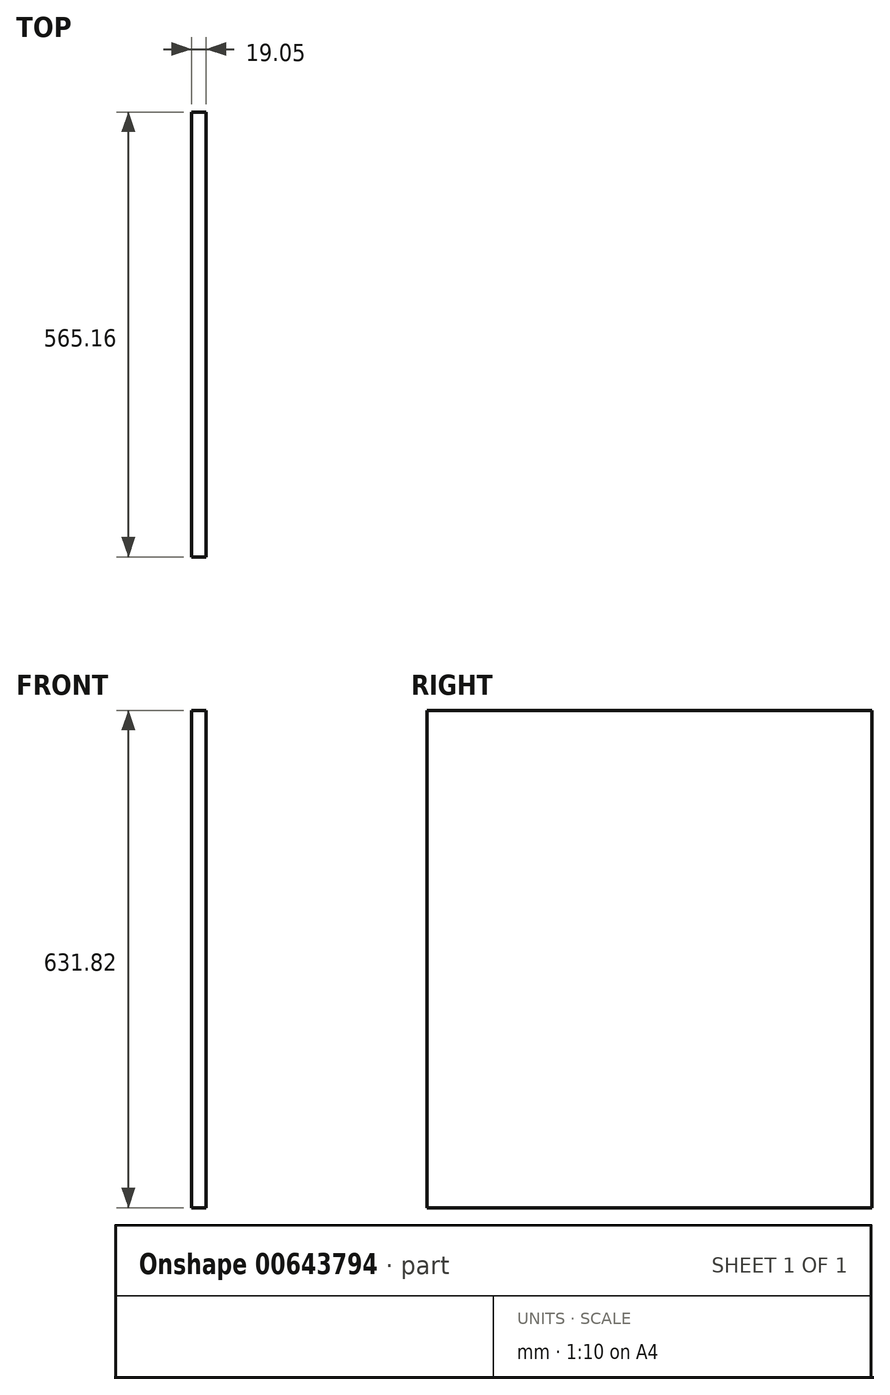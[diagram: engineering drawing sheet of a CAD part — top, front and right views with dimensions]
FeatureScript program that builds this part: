
annotation { "Feature Type Name" : "Feature", "Feature Type Description" : "" }
export const myFeature = defineFeature(function(context is Context, id is Id, definition is map)
    precondition{}
    {
        {
            var Q0;
            Q0=qCreatedBy(makeId("Right.planeOp"),FACE);
            var sketch = newSketch(context, id + "F0", { "sketchPlane" : qUnion([Q0])});
            skLineSegment(sketch, "E0.bottom", {"start": v(282.57, 315.91) * mm, "end": v(-282.58, 315.91) * mm});
            skLineSegment(sketch, "E0.top", {"start": v(282.57, -315.91) * mm, "end": v(-282.58, -315.91) * mm});
            skLineSegment(sketch, "E0.left", {"start": v(282.58, 315.91) * mm, "end": v(282.57, -315.91) * mm});
            skLineSegment(sketch, "E0.right", {"start": v(-282.58, 315.91) * mm, "end": v(-282.58, -315.91) * mm});
            skPoint(sketch, "E0.middle", {"position": v(0, 0) * mm});
            skSolve(sketch);
        }
        {
            var Q0;
            Q0=makeQuery(id+"F0.imprint","IMPRINT",FACE,{"disambiguationData":[TD([[makeQuery(id+"F0.imprint","IMPRINT",EDGE,{"derivedFrom":sQuery(id+"F0.wireOp",EDGE,"E0.bottom")}),1.0]])]});
            extrude(context, id + "F1", {"entities" : qUnion([Q0]), "depth" : 19.05 * mm, "offsetDistance" : 25.4 * mm});
        }
    });
